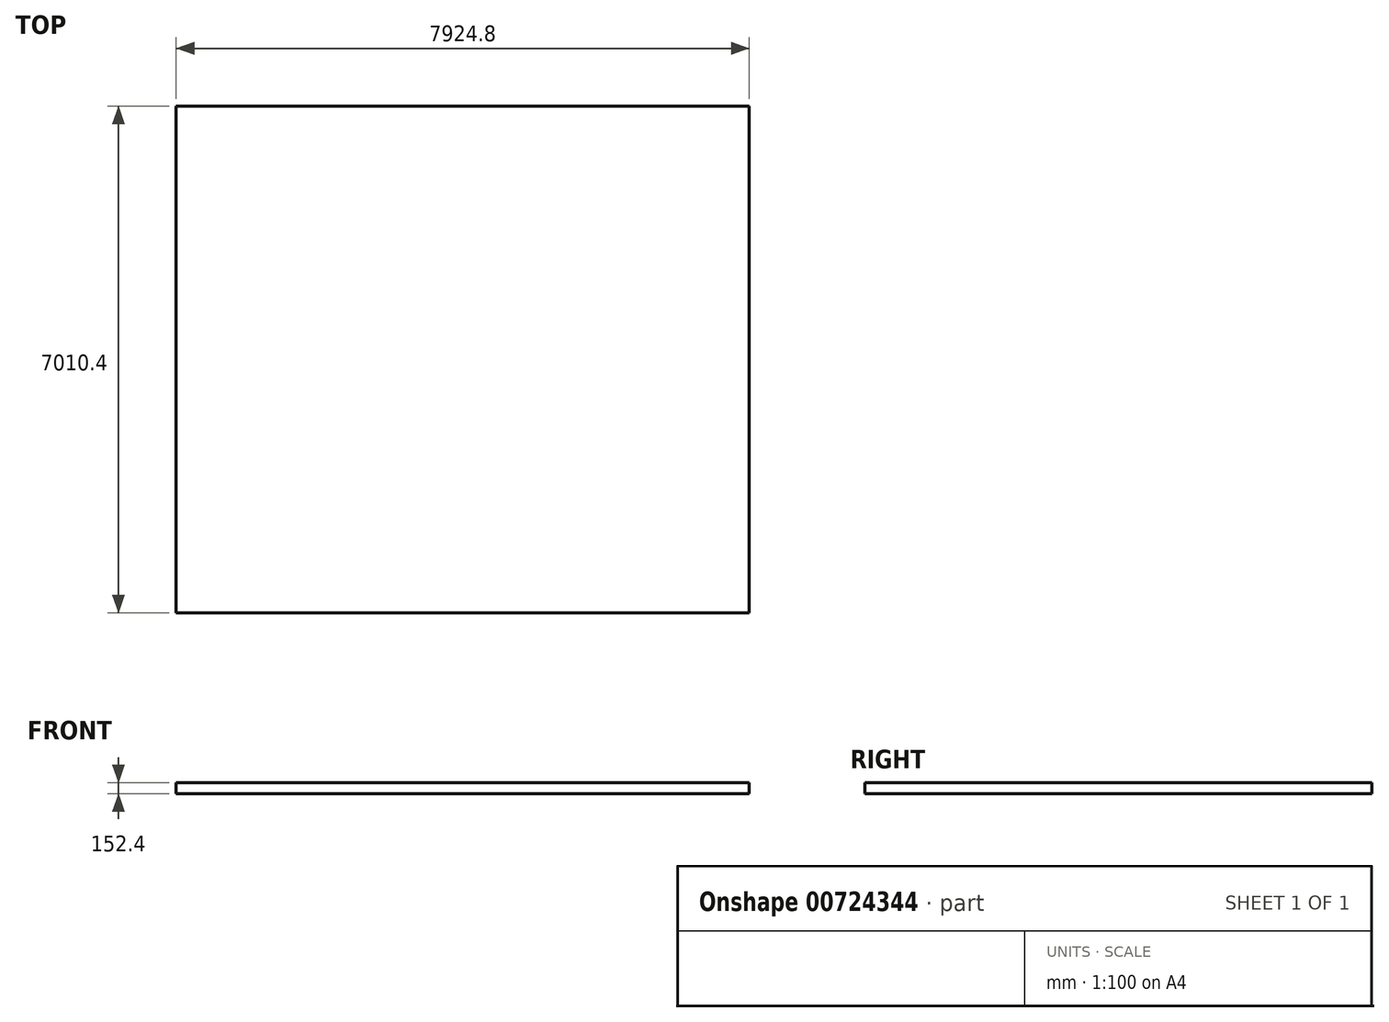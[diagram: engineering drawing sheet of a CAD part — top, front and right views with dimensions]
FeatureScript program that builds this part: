
annotation { "Feature Type Name" : "Feature", "Feature Type Description" : "" }
export const myFeature = defineFeature(function(context is Context, id is Id, definition is map)
    precondition{}
    {
        {
            var Q0;
            Q0=qCreatedBy(makeId("Top.planeOp"),FACE);
            var sketch = newSketch(context, id + "F0", { "sketchPlane" : qUnion([Q0])});
            skLineSegment(sketch, "E0.bottom", {"start": v(-3962.4, 3505.2) * mm, "end": v(3962.4, 3505.2) * mm});
            skLineSegment(sketch, "E0.top", {"start": v(-3962.4, -3505.2) * mm, "end": v(3962.4, -3505.2) * mm});
            skLineSegment(sketch, "E0.left", {"start": v(-3962.4, 3505.2) * mm, "end": v(-3962.4, -3505.2) * mm});
            skLineSegment(sketch, "E0.right", {"start": v(3962.4, 3505.2) * mm, "end": v(3962.4, -3505.2) * mm});
            skPoint(sketch, "E0.middle", {"position": v(0, 0) * mm});
            skSolve(sketch);
        }
        {
            var Q0;
            Q0=makeQuery(id+"F0.imprint","IMPRINT",FACE,{"disambiguationData":[TD([[makeQuery(id+"F0.imprint","IMPRINT",EDGE,{"derivedFrom":sQuery(id+"F0.wireOp",EDGE,"E0.bottom")}),-1.0]])]});
            extrude(context, id + "F1", {"entities" : qUnion([Q0]), "depth" : 152.4 * mm, "offsetDistance" : 25.4 * mm});
        }
    });
